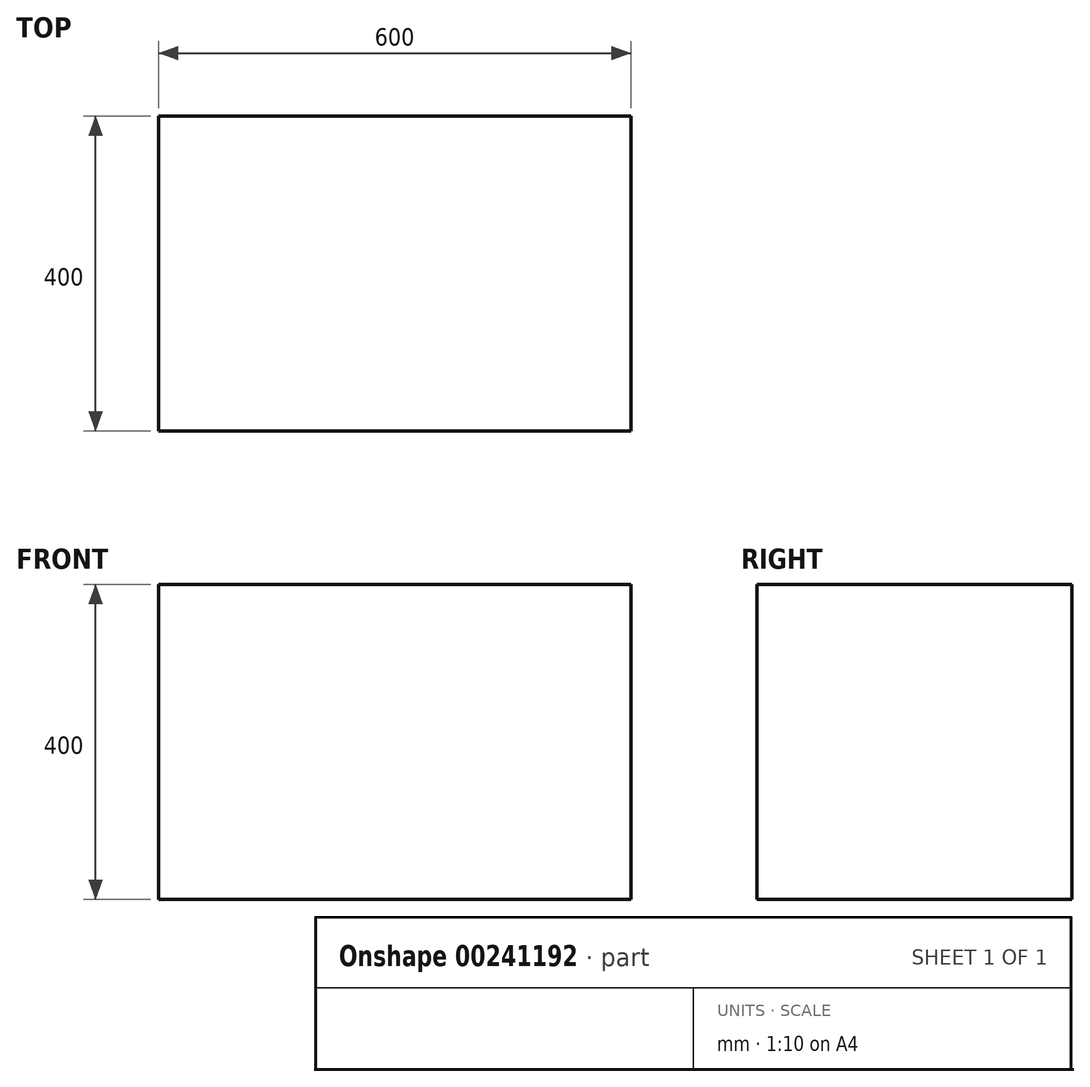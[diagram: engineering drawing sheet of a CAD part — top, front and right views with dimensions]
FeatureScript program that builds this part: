
annotation { "Feature Type Name" : "Feature", "Feature Type Description" : "" }
export const myFeature = defineFeature(function(context is Context, id is Id, definition is map)
    precondition{}
    {
        {
            var Q0;
            Q0=qCreatedBy(makeId("Front.planeOp"),FACE);
            var sketch = newSketch(context, id + "F0", { "sketchPlane" : qUnion([Q0])});
            skLineSegment(sketch, "E0.bottom", {"start": v(-539.64, 405.47) * mm, "end": v(60.36, 405.47) * mm});
            skLineSegment(sketch, "E0.top", {"start": v(-539.64, 5.47) * mm, "end": v(60.36, 5.47) * mm});
            skLineSegment(sketch, "E0.left", {"start": v(-539.64, 405.47) * mm, "end": v(-539.64, 5.47) * mm});
            skLineSegment(sketch, "E0.right", {"start": v(60.36, 405.47) * mm, "end": v(60.36, 5.47) * mm});
            skSolve(sketch);
        }
        {
            var Q0;
            Q0=makeQuery(id+"F0.imprint","IMPRINT",FACE,{"disambiguationData":[TD([[makeQuery(id+"F0.imprint","IMPRINT",EDGE,{"derivedFrom":sQuery(id+"F0.wireOp",EDGE,"E0.bottom")}),-1.0]])]});
            extrude(context, id + "F1", {"entities" : qUnion([Q0]), "depth" : 400 * mm});
        }
    });
